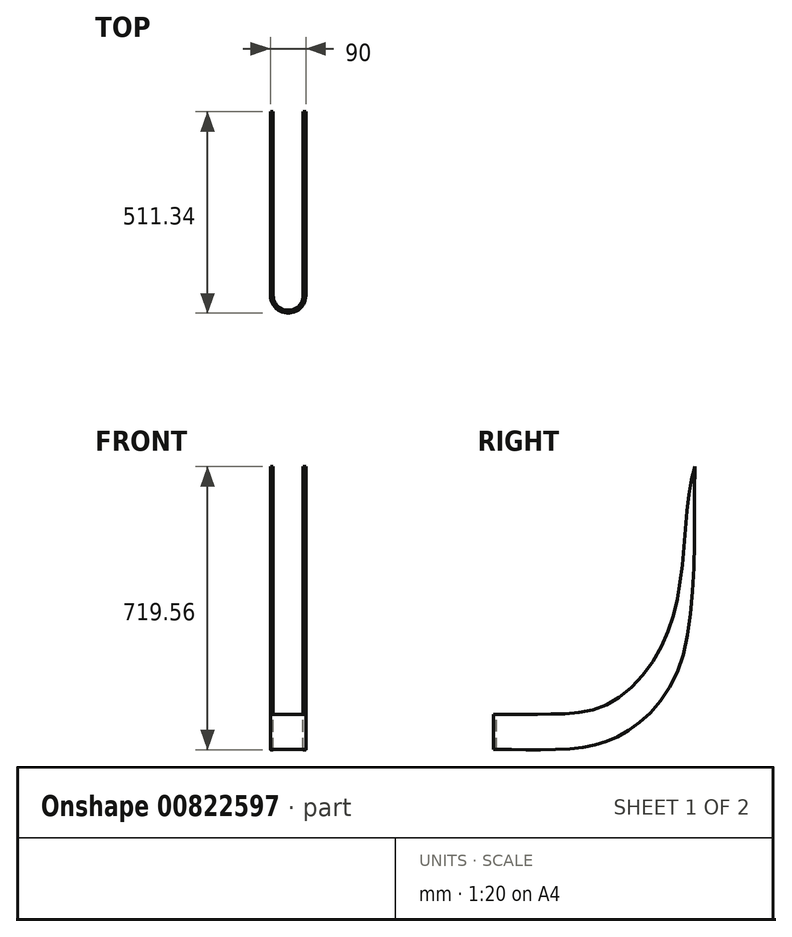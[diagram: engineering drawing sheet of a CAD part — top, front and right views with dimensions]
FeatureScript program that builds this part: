
annotation { "Feature Type Name" : "Feature", "Feature Type Description" : "" }
export const myFeature = defineFeature(function(context is Context, id is Id, definition is map)
    precondition{}
    {
        {
            var Q0;
            Q0=qCreatedBy(makeId("Right.planeOp"),FACE);
            var sketch = newSketch(context, id + "F0", { "sketchPlane" : qUnion([Q0])});
            skFitSpline(sketch, "E0", {"points": [v(0, 0) * mm, v(190.31, 2.01) * mm, v(330.46, 40.83) * mm, v(470.96, 209.52) * mm, v(511.34, 719.1) * mm], "startDerivative": vector(699.54, 8.95) * mm, "endDerivative": vector(35.48, 1595.38) * mm});
            skFitSpline(sketch, "E1", {"points": [v(0, 90) * mm, v(131.36, 90) * mm, v(288.33, 114.37) * mm, v(430.64, 271.6) * mm, v(482.38, 503.1) * mm, v(511.34, 719.1) * mm], "startDerivative": vector(698.72, -26.07) * mm, "endDerivative": vector(237.93, 701.56) * mm});
            skLineSegment(sketch, "E2", {"start": v(0, 90) * mm, "end": v(0, 0) * mm});
            skSolve(sketch);
        }
        {
            var Q0;
            Q0=makeQuery(id+"F0.imprint","IMPRINT",FACE,{"disambiguationData":[TD([[makeQuery(id+"F0.imprint","IMPRINT",EDGE,{"derivedFrom":sQuery(id+"F0.wireOp",EDGE,"E0")}),1.0]])]});
            extrude(context, id + "F1", {"entities" : qUnion([Q0]), "depth" : 90 * mm, "offsetDistance" : 25.4 * mm});
        }
        {
            var Q0;
            Q0=qCreatedBy(makeId("Top.planeOp"),FACE);
            cPlane(context, id + "F2", {"entities" : qUnion([Q0]), "cplaneType" : CPlaneType.OFFSET, "offset" : 919.48 * mm, "width" : 152.4 * mm, "height" : 152.4 * mm});
        }
        {
            var Q0;
            Q0=qCreatedBy(id+"F2.planeOp",FACE);
            var sketch = newSketch(context, id + "F3", { "sketchPlane" : qUnion([Q0])});
            skFitSpline(sketch, "E3.0.0", {"points": [v(0, 511.34) * mm, v(0, 494.32) * mm, v(0, 484.85) * mm, v(0, 454.3) * mm, v(0, 301.1) * mm, v(0, 133.76) * mm, v(0, 38.8) * mm, v(0, 0) * mm]});
            skLineSegment(sketch, "E3.0.1", {"start": v(0, 0) * mm, "end": v(90, 0) * mm});
            skFitSpline(sketch, "E3.0.2", {"points": [v(90, 0) * mm, v(90, 38.8) * mm, v(90, 133.76) * mm, v(90, 301.1) * mm, v(90, 454.3) * mm, v(90, 484.85) * mm, v(90, 494.32) * mm, v(90, 511.34) * mm]});
            skLineSegment(sketch, "E3.0.3", {"start": v(90, 511.34) * mm, "end": v(0, 511.34) * mm});
            skLineSegment(sketch, "E4", {"start": v(0, 511.34) * mm, "end": v(0, 573.03) * mm});
            skLineSegment(sketch, "E5", {"start": v(0, 573.03) * mm, "end": v(7, 573.03) * mm});
            skLineSegment(sketch, "E6", {"start": v(7, 573.03) * mm, "end": v(7, 45) * mm});
            skLineSegment(sketch, "E7", {"start": v(90, 511.34) * mm, "end": v(90, 587.3) * mm});
            skLineSegment(sketch, "E8", {"start": v(90, 587.3) * mm, "end": v(83, 587.3) * mm});
            skLineSegment(sketch, "E9", {"start": v(83, 587.3) * mm, "end": v(83, 45) * mm});
            skArc(sketch, "E10", {"start": v(7, 45) * mm, "mid": v(45, 7) * mm, "end": v(83, 45) * mm});
            skArc(sketch, "E11", {"start": v(0, 45) * mm, "mid": v(45, 0) * mm, "end": v(90, 45) * mm});
            skSolve(sketch);
        }
        {
            var Q0;
            {var subQ0=sQuery(id+"F3.wireOp",EDGE,"E3.0.1");var subQ1=sQuery(id+"F3.wireOp",EDGE,"E3.0.0");var subQ2=makeQuery(id+"F3.imprint","INTERSECT",VERTEX,{"derivedFrom":[subQ1,subQ0]});Q0=makeQuery(id+"F3.imprint","IMPRINT",FACE,{"disambiguationData":[TD([[makeQuery(id+"F3.imprint","IMPRINT",EDGE,{"disambiguationData":[TD([[subQ2,1.0]])],"derivedFrom":subQ1}),1.0]])]});}
            var Q1;
            {var subQ0=sQuery(id+"F3.wireOp",EDGE,"E3.0.2");var subQ1=sQuery(id+"F3.wireOp",EDGE,"E3.0.1");var subQ2=makeQuery(id+"F3.imprint","INTERSECT",VERTEX,{"derivedFrom":[subQ1,subQ0]});Q1=makeQuery(id+"F3.imprint","IMPRINT",FACE,{"disambiguationData":[TD([[makeQuery(id+"F3.imprint","IMPRINT",EDGE,{"disambiguationData":[TD([[subQ2,1.0]])],"derivedFrom":subQ1}),1.0]])]});}
            var Q2;
            {var subQ5=sQuery(id+"F3.wireOp",EDGE,"E10");Q2=makeQuery(id+"F3.imprint","IMPRINT",FACE,{"disambiguationData":[TD([[makeQuery(id+"F3.imprint","IMPRINT",EDGE,{"derivedFrom":subQ5}),1.0]])]});}
            extrude(context, id + "F4", {"entities" : qUnion([Q0, Q1, Q2]), "operationType" : NewBodyOperationType.REMOVE, "oppositeDirection" : true, "depth" : 962.66 * mm, "offsetDistance" : 25.4 * mm});
        }
    });
